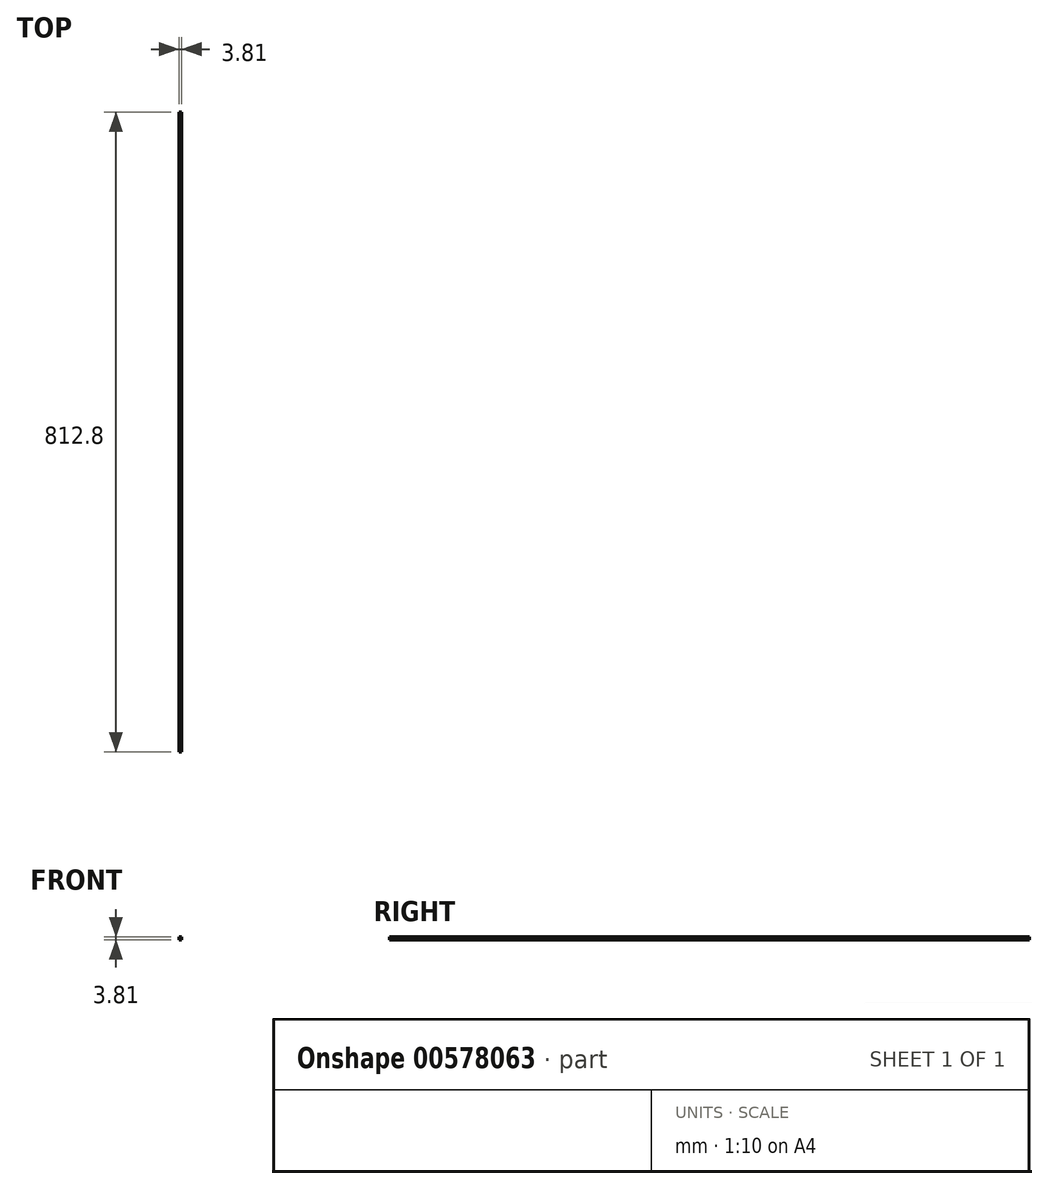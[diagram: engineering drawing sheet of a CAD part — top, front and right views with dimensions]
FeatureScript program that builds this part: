
annotation { "Feature Type Name" : "Feature", "Feature Type Description" : "" }
export const myFeature = defineFeature(function(context is Context, id is Id, definition is map)
    precondition{}
    {
        {
            var Q0;
            Q0=qCreatedBy(makeId("Top.planeOp"),FACE);
            var sketch = newSketch(context, id + "F0", { "sketchPlane" : qUnion([Q0])});
            skLineSegment(sketch, "E0.bottom", {"start": v(-38.52, 826.02) * mm, "end": v(-34.7, 826.02) * mm});
            skLineSegment(sketch, "E0.top", {"start": v(-38.52, 13.22) * mm, "end": v(-34.7, 13.22) * mm});
            skLineSegment(sketch, "E0.left", {"start": v(-38.52, 826.02) * mm, "end": v(-38.52, 13.22) * mm});
            skLineSegment(sketch, "E0.right", {"start": v(-34.7, 826.02) * mm, "end": v(-34.7, 13.22) * mm});
            skSolve(sketch);
        }
        {
            var Q0;
            Q0=makeQuery(id+"F0.imprint","IMPRINT",FACE,{"disambiguationData":[TD([[makeQuery(id+"F0.imprint","IMPRINT",EDGE,{"derivedFrom":sQuery(id+"F0.wireOp",EDGE,"E0.bottom")}),-1.0]])]});
            extrude(context, id + "F1", {"entities" : qUnion([Q0]), "depth" : 3.8 * mm, "offsetDistance" : 25.4 * mm});
        }
    });
